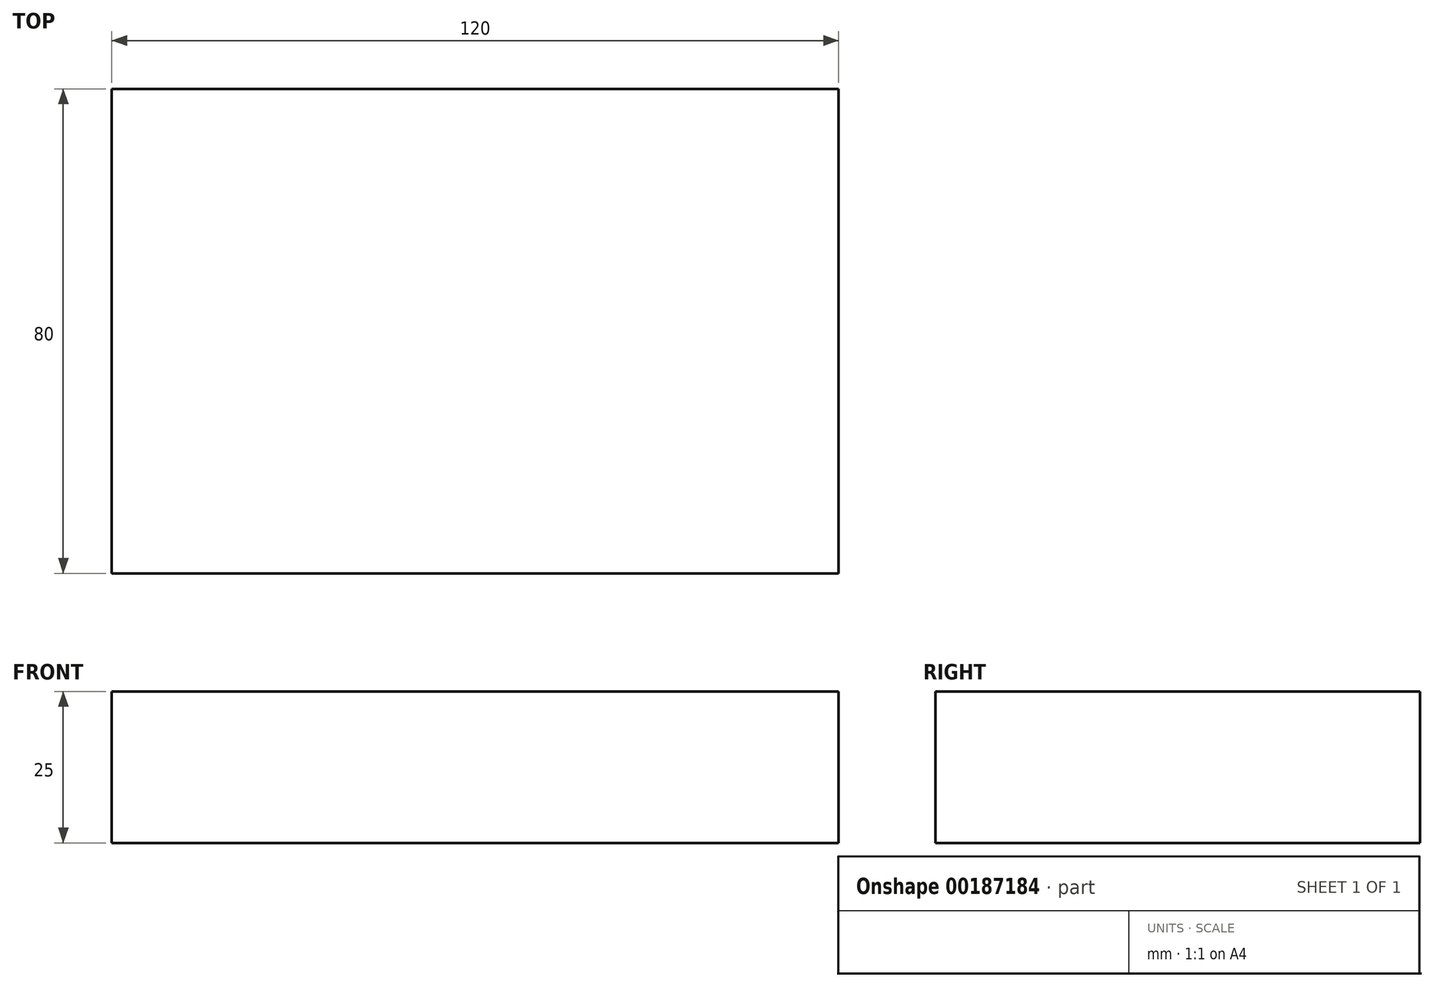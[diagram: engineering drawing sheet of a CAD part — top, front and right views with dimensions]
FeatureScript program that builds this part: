
annotation { "Feature Type Name" : "Feature", "Feature Type Description" : "" }
export const myFeature = defineFeature(function(context is Context, id is Id, definition is map)
    precondition{}
    {
        {
            var Q0;
            Q0=qCreatedBy(makeId("Top.planeOp"),FACE);
            var sketch = newSketch(context, id + "F0", { "sketchPlane" : qUnion([Q0])});
            skLineSegment(sketch, "E0.bottom", {"start": v(-60, 40) * mm, "end": v(60, 40) * mm});
            skLineSegment(sketch, "E0.top", {"start": v(-60, -40) * mm, "end": v(60, -40) * mm});
            skLineSegment(sketch, "E0.left", {"start": v(-60, 40) * mm, "end": v(-60, -40) * mm});
            skLineSegment(sketch, "E0.right", {"start": v(60, 40) * mm, "end": v(60, -40) * mm});
            skPoint(sketch, "E0.middle", {"position": v(0, 0) * mm});
            skSolve(sketch);
        }
        {
            var Q0;
            Q0 = qSketchRegion(id + "F0", true);
            extrude(context, id + "F1", {"entities" : qUnion([Q0]), "depth" : 25 * mm});
        }
    });
